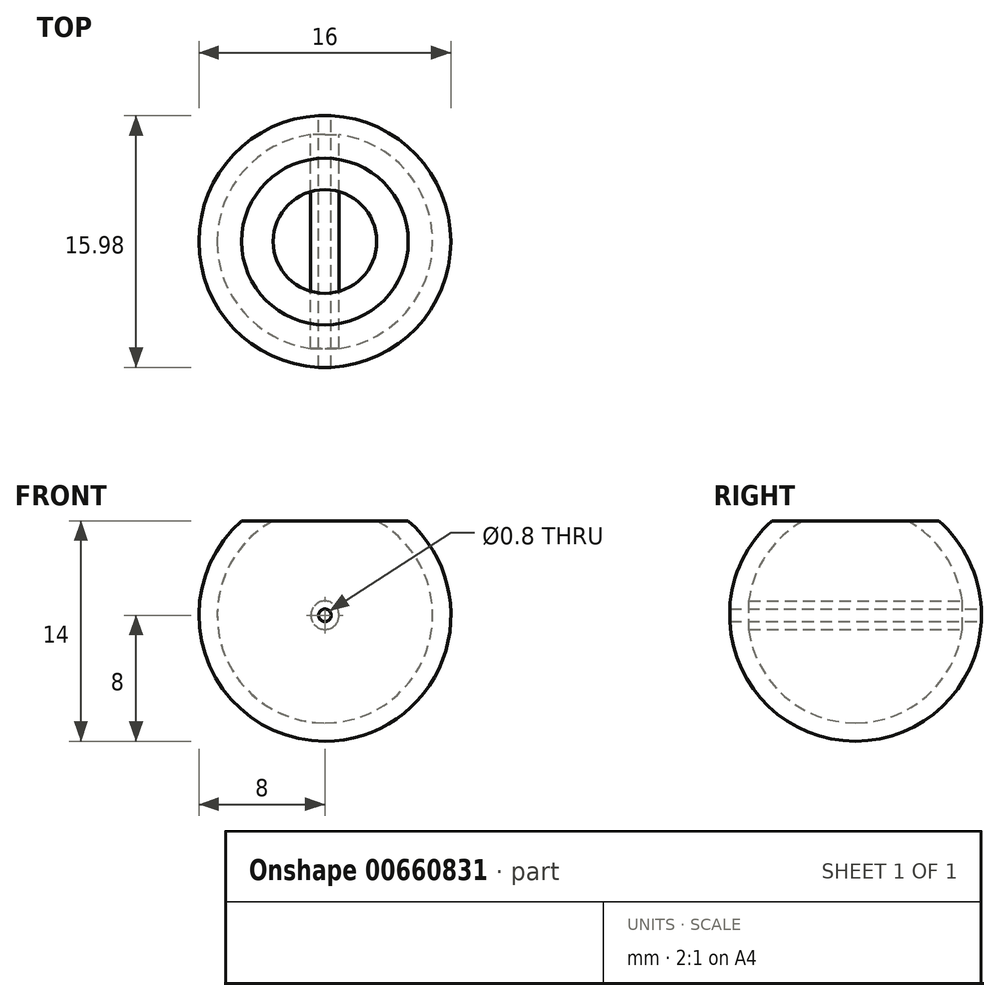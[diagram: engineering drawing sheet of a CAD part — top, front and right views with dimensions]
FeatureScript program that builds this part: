
annotation { "Feature Type Name" : "Feature", "Feature Type Description" : "" }
export const myFeature = defineFeature(function(context is Context, id is Id, definition is map)
    precondition{}
    {
        {
            var Q0;
            Q0=qCreatedBy(makeId("Front.planeOp"),FACE);
            var sketch = newSketch(context, id + "F0", { "sketchPlane" : qUnion([Q0])});
            skLineSegment(sketch, "E0", {"start": v(0, 0) * mm, "end": v(0, 23.94) * mm, "construction": true});
            skArc(sketch, "E1", {"start": v(-5.3, 14) * mm, "mid": v(-7.48, 5.17) * mm, "end": v(0, 0) * mm});
            skLineSegment(sketch, "E2", {"start": v(-5.3, 14) * mm, "end": v(-3.3, 14) * mm});
            skArc(sketch, "E3", {"start": v(-3.3, 14) * mm, "mid": v(-6.63, 6.3) * mm, "end": v(0, 1.16) * mm});
            skLineSegment(sketch, "E4", {"start": v(0, 1.16) * mm, "end": v(0, 0) * mm});
            skLineSegment(sketch, "E5", {"start": v(0, 0) * mm, "end": v(-15.27, 0) * mm, "construction": true});
            skSolve(sketch);
        }
        {
            var Q0;
            Q0 = qSketchRegion(id + "F0", true);
            var Q1;
            Q1=sQuery(id+"F0.wireOp",EDGE,"E0");
            revolve(context, id + "F1", {"entities" : qUnion([Q0]), "axis" : qUnion([Q1]), "revolveType" : RevolveType.FULL});
        }
        {
            var Q0;
            Q0=qCreatedBy(makeId("Front.planeOp"),FACE);
            var sketch = newSketch(context, id + "F2", { "sketchPlane" : qUnion([Q0])});
            skCircle(sketch, "E6", {"center": v(0, 8) * mm, "radius": 0.4 * mm});
            skCircle(sketch, "E7", {"center": v(0, 8) * mm, "radius": 0.9 * mm});
            skSolve(sketch);
        }
        {
            var Q0;
            Q0 = qSketchRegion(id + "F2", true);
            var Q1;
            Q1=makeQuery(id+"F1.opRevolve","SWEPT_FACE",FACE,{"disambiguationData":[OSD([sQuery(id+"F0.wireOp",EDGE,"E1")])]});
            var Q2;
            Q2=makeQuery(id+"F1.opRevolve","SWEPT_FACE",FACE,{"disambiguationData":[OSD([sQuery(id+"F0.wireOp",EDGE,"E1")])]});
            extrude(context, id + "F3", {"entities" : qUnion([Q0]), "operationType" : NewBodyOperationType.ADD, "endBound" : BoundingType.UP_TO_SURFACE, "depth" : 25 * mm, "endBoundEntityFace" : qUnion([Q1]), "offsetDistance" : 25 * mm, "hasSecondDirection" : true, "secondDirectionBound" : SecondDirectionBoundingType.UP_TO_SURFACE, "secondDirectionOppositeDirection" : true, "secondDirectionDepth" : 25 * mm, "secondDirectionBoundEntityFace" : qUnion([Q2])});
        }
        {
            var Q0;
            Q0=qCreatedBy(makeId("Front.planeOp"),FACE);
            var sketch = newSketch(context, id + "F4", { "sketchPlane" : qUnion([Q0])});
            skCircle(sketch, "E8", {"center": v(0, 8) * mm, "radius": 0.4 * mm});
            skSolve(sketch);
        }
        {
            var Q0;
            Q0 = qSketchRegion(id + "F4", true);
            extrude(context, id + "F5", {"entities" : qUnion([Q0]), "operationType" : NewBodyOperationType.REMOVE, "endBound" : BoundingType.THROUGH_ALL, "oppositeDirection" : true, "depth" : 25 * mm, "offsetDistance" : 25 * mm, "hasSecondDirection" : true, "secondDirectionBound" : SecondDirectionBoundingType.THROUGH_ALL, "secondDirectionOppositeDirection" : false, "secondDirectionDepth" : 25 * mm});
        }
    });
